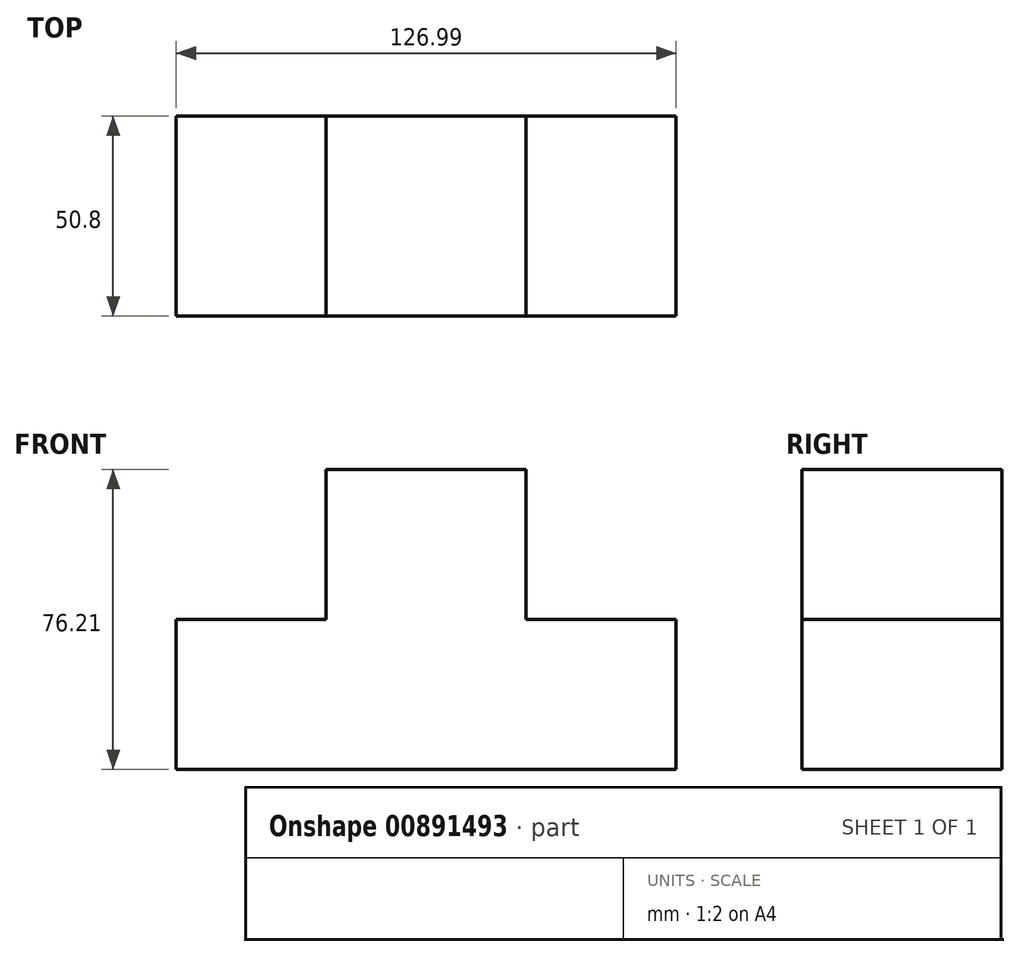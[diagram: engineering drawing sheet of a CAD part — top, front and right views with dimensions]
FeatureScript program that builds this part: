
annotation { "Feature Type Name" : "Feature", "Feature Type Description" : "" }
export const myFeature = defineFeature(function(context is Context, id is Id, definition is map)
    precondition{}
    {
        {
            var Q0;
            Q0=qCreatedBy(makeId("Front.planeOp"),FACE);
            var sketch = newSketch(context, id + "F0", { "sketchPlane" : qUnion([Q0])});
            skLineSegment(sketch, "E0", {"start": v(-53.2, -33.62) * mm, "end": v(73.8, -33.62) * mm});
            skLineSegment(sketch, "E1", {"start": v(73.8, -33.62) * mm, "end": v(73.8, 42.59) * mm});
            skLineSegment(sketch, "E2", {"start": v(73.8, 42.59) * mm, "end": v(-53.2, 42.59) * mm});
            skLineSegment(sketch, "E3", {"start": v(-53.2, 42.59) * mm, "end": v(-53.2, -33.62) * mm});
            skSolve(sketch);
        }
        {
            var Q0;
            Q0 = qSketchRegion(id + "F0", true);
            extrude(context, id + "F1", {"entities" : qUnion([Q0]), "depth" : 50.8 * mm, "offsetDistance" : 25.4 * mm});
        }
        {
            var Q0;
            Q0=makeQuery(id+"F1.opExtrude","CAP_FACE",FACE,{"disambiguationData":[OSD([sQuery(id+"F0.wireOp",EDGE,"E0"),sQuery(id+"F0.wireOp",EDGE,"E1"),sQuery(id+"F0.wireOp",EDGE,"E2"),sQuery(id+"F0.wireOp",EDGE,"E3")])],"isStart":false});
            var sketch = newSketch(context, id + "F2", { "sketchPlane" : qUnion([Q0])});
            skLineSegment(sketch, "E4", {"start": v(73.8, 42.59) * mm, "end": v(73.8, 4.48) * mm});
            skLineSegment(sketch, "E5", {"start": v(73.8, 4.48) * mm, "end": v(35.7, 4.48) * mm});
            skLineSegment(sketch, "E6", {"start": v(35.7, 4.48) * mm, "end": v(35.7, 42.59) * mm});
            skLineSegment(sketch, "E7", {"start": v(35.7, 42.59) * mm, "end": v(73.8, 42.59) * mm});
            skSolve(sketch);
        }
        {
            var Q0;
            Q0 = qSketchRegion(id + "F2", true);
            extrude(context, id + "F3", {"entities" : qUnion([Q0]), "operationType" : NewBodyOperationType.REMOVE, "oppositeDirection" : true, "depth" : 50.8 * mm, "offsetDistance" : 25.4 * mm});
        }
        {
            var Q0;
            Q0=makeQuery(id+"F1.opExtrude","CAP_FACE",FACE,{"disambiguationData":[OSD([sQuery(id+"F0.wireOp",EDGE,"E0"),sQuery(id+"F0.wireOp",EDGE,"E1"),sQuery(id+"F0.wireOp",EDGE,"E2"),sQuery(id+"F0.wireOp",EDGE,"E3")])],"isStart":false});
            var sketch = newSketch(context, id + "F4", { "sketchPlane" : qUnion([Q0])});
            skLineSegment(sketch, "E8", {"start": v(-53.2, 42.59) * mm, "end": v(-53.2, 4.48) * mm});
            skLineSegment(sketch, "E9", {"start": v(-53.2, 4.48) * mm, "end": v(-15.1, 4.48) * mm});
            skLineSegment(sketch, "E10", {"start": v(-15.1, 4.48) * mm, "end": v(-15.1, 42.59) * mm});
            skLineSegment(sketch, "E11", {"start": v(-15.1, 42.59) * mm, "end": v(-53.2, 42.59) * mm});
            skSolve(sketch);
        }
        {
            var Q0;
            Q0 = qSketchRegion(id + "F4", true);
            extrude(context, id + "F5", {"entities" : qUnion([Q0]), "operationType" : NewBodyOperationType.REMOVE, "oppositeDirection" : true, "depth" : 50.8 * mm, "offsetDistance" : 25.4 * mm});
        }
    });
